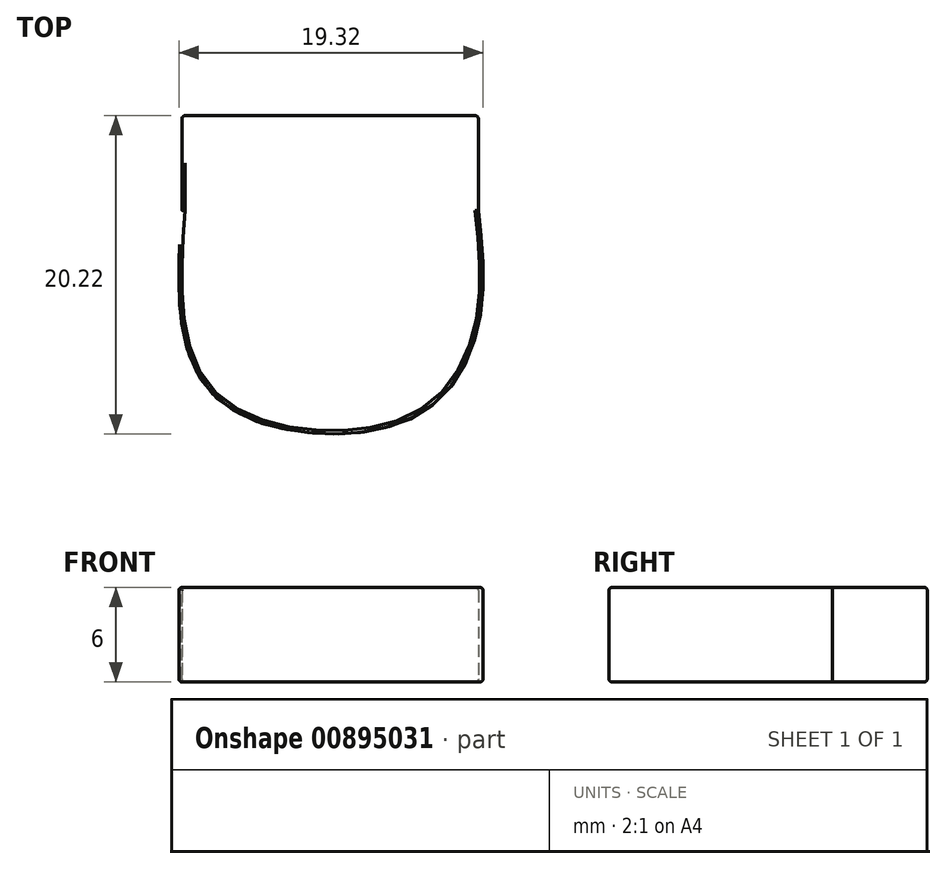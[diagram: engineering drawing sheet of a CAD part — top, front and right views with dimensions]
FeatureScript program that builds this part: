
annotation { "Feature Type Name" : "Feature", "Feature Type Description" : "" }
export const myFeature = defineFeature(function(context is Context, id is Id, definition is map)
    precondition{}
    {
        {
            var Q0;
            Q0=qCreatedBy(makeId("Top.planeOp"),FACE);
            var sketch = newSketch(context, id + "F0", { "sketchPlane" : qUnion([Q0])});
            skFitSpline(sketch, "E0", {"points": [v(9.41, 3.57) * mm, v(9.41, -3.7) * mm, v(5.2, -9.6) * mm, v(-5.2, -9.6) * mm, v(-9.41, -3.7) * mm, v(-9.41, 3.57) * mm, v(-9.41, 3.57) * mm, v(-9.41, 3.57) * mm, v(-9.41, 5.08) * mm, v(-9.41, 6.59) * mm]});
            skFitSpline(sketch, "E1", {"points": [v(-9.41, 6.59) * mm, v(-9.41, 8.04) * mm, v(-9.41, 9.52) * mm, v(-9.41, 9.6) * mm, v(-9.41, 9.6) * mm, v(-9.41, 9.6) * mm]});
            skFitSpline(sketch, "E2", {"points": [v(-9.41, 9.6) * mm, v(-9.41, 9.6) * mm, v(-9.41, 9.6) * mm, v(-9.17, 9.6) * mm, v(9.17, 9.6) * mm, v(9.41, 9.6) * mm, v(9.41, 9.6) * mm, v(9.41, 9.6) * mm]});
            skFitSpline(sketch, "E3", {"points": [v(9.41, 9.6) * mm, v(9.41, 9.6) * mm, v(9.41, 9.6) * mm, v(9.41, 9.44) * mm, v(9.41, 3.73) * mm, v(9.41, 3.57) * mm, v(9.41, 3.57) * mm, v(9.41, 3.57) * mm]});
            skSolve(sketch);
        }
        {
            var Q0;
            Q0=makeQuery(id+"F0.imprint","IMPRINT",FACE,{"disambiguationData":[TD([[makeQuery(id+"F0.imprint","IMPRINT",EDGE,{"derivedFrom":sQuery(id+"F0.wireOp",EDGE,"E0")}),-1.0]])]});
            extrude(context, id + "F1", {"entities" : qUnion([Q0]), "depth" : 6 * mm, "offsetDistance" : 25 * mm});
        }
        {
            var Q0;
            Q0=makeQuery(id+"F1.opExtrude","CAP_FACE",FACE,{"disambiguationData":[OSD([sQuery(id+"F0.wireOp",EDGE,"E0"),sQuery(id+"F0.wireOp",EDGE,"E1"),sQuery(id+"F0.wireOp",EDGE,"E2"),sQuery(id+"F0.wireOp",EDGE,"E3")])],"isStart":true});
            var Q1;
            Q1=makeQuery(id+"F1.opExtrude","CAP_FACE",FACE,{"disambiguationData":[OSD([sQuery(id+"F0.wireOp",EDGE,"E0"),sQuery(id+"F0.wireOp",EDGE,"E1"),sQuery(id+"F0.wireOp",EDGE,"E2"),sQuery(id+"F0.wireOp",EDGE,"E3")])],"isStart":false});
            fillet(context, id + "F2", {"entities" : qUnion([Q0, Q1]), "radius" : 0.2 * mm, "tangentPropagation" : true, "allowEdgeOverflow" : false});
        }
        {
            var Q0;
            Q0=makeQuery(id+"F1.opExtrude","SWEPT_EDGE",EDGE,{"disambiguationData":[OSD([sQuery(id+"F0.wireOp",EDGE,"E1"),sQuery(id+"F0.wireOp",EDGE,"E2")])]});
            var Q1;
            Q1=makeQuery(id+"F1.opExtrude","SWEPT_EDGE",EDGE,{"disambiguationData":[OSD([sQuery(id+"F0.wireOp",EDGE,"E2"),sQuery(id+"F0.wireOp",EDGE,"E3")])]});
            fillet(context, id + "F3", {"entities" : qUnion([Q0, Q1]), "radius" : 0.2 * mm, "tangentPropagation" : true, "allowEdgeOverflow" : false});
        }
    });
